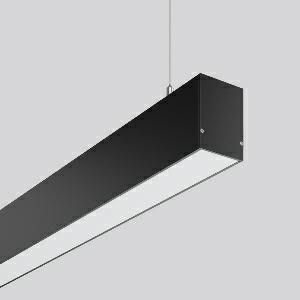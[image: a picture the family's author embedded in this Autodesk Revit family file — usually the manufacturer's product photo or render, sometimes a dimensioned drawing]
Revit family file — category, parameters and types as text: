
# Revit family: less_is_more_50_312314_003_76_c28b
name_source: partatom
category: Lighting Fixtures
units: mm (PartAtom-declared; Revit-internal decimal feet)

## family parameters
Cut with Voids When Loaded = No
Host = Face
Light Source = No
Part Type = Normal
Room Calculation Point = No
Round Connector Dimension = Use Diameter
Shared = No

## types (1)
- LESS IS MORE 50 (1 x LED Modul 830, 4650 lm, 3000)
    Apparent Load = 40 VA
    CIE Flux Codes = 48 79 95 100 100
    Color Rendering = 80
    Color Temperature = 3000
    Default Elevation = 1800 mm
    Description = Series: LESS IS MORE 50
Linear pendant luminaire for aesthetically sophisticated lighting. Housing: extruded aluminium profile, powder-coated. End cap aluminium powder-coated. Canopy made of aluminium, powder-coated. Diffuser made of non-yellowing plastic (PMMA), opal. Direct light emission. Suitable for pendant. 2-point steel cable suspension freely positionable and infinitely height-adjustable. Special lengths available on request. LED unit with integrated converter interchangeable and removable. Suitable for through-wiring. With sensors or as a safety luminaire on request. 
Colour: deep black, matt (RAL 9005)
Length: 1687 mm
Width: 57 mm
Height: 75 mm
Suspension length: 2000 mm
Lamp: LED
Socket: without socket
Colour temperature: 3000K
Colour rendering index (CRI): 80
System power: 40 W
Rated luminous flux: 4650 lm
Luminous efficiency: 116 lm/W
Control gear: Converter, dimmable, DALI
Protection class: I
Type of protection: IP 20
    Height = 75 mm
    Lamp = 1 x LED Modul 830
    Lamp Light Flux = 4650 lm
    Lamp count = 1
    Length = 1687 mm
    Lifetime = 50000 h
    Luminous efficacy = 116 lm/W
    Manufacturer = RZB
    ModVariant = No
    Model = 312314.003.76
    Mounting Place = Ceiling
    Mounting Type = Pendant
    Number of Poles = 1
    OnlyDefault = Yes
    Power Factor = 1
    Product Name = LESS IS MORE 50
    Product group = Pendant LED linear luminaires
    ProductGroupID = 907
    Protection Class = Protection class I
    Protection Degree = IP 20
    RLX_Detail_Level = 1
    RLX_Emergency_Light_Flux = 0 lm
    RLX_Emergency_Type = 0
    RLX_Emergency_Type_DB = No
    RlxData = <blob elided: 28877 chars, md5=00a78cdd>
    Socket = socket
    Standby Power = 0 W
    System Light Flux = 4650 lm
    System Power = 40 W
    Type Comments = Product without accessories
    Type Image = 312318.003.jpg
    URL = http://relux.com
    VarID = ---
    Voltage = 230 V
    Voltage Range = 220-240 V
    Weight = 0.00 kg
    Width = 57 mm

## geometry (parser evidence)
native form markers: Blend x4, Sweep x9
no freeform markers — native parametric forms only
